# Revit family: PRD_AR_FlshCntrlDvcs_F5EWcFlushValve_F5EF4002
name_source: partatom
category: Plumbing Fixtures
units: mm (PartAtom-declared; Revit-internal decimal feet)

## family parameters
Cut with Voids When Loaded = Yes
Enable Cutting in Views = Yes
Host = Face
Maintain Annotation Orientation = No
OmniClass Number = 23.45.55.11
OmniClass Title = Sanitary Components
Part Type = Normal
Room Calculation Point = No
Round Connector Dimension = Use Diameter
Shared = No

## types (1)
- F5EF4002
    AssetType = Fixed
    BIMObjectName = PRD_AR_FlushControlDevices_F5EWcFlushValve_F5EF4002
    BodyMaterial = PRD_AR_PolishedChromium_PlatedBrass
    BottomMaterial = PRD_AR_Plastic_Black
    CW Connection = Yes
    CWFU = 0
    CalculationFlowRateColdWater = 1 l/s
    Category = Pr_75_50_46_31, Flush control devices
    CloseOffRating = 0.0 Pa
    DN = 20 mm  [stored 0.0656168 ft]
    Default Elevation = 1219 mm
    DefaultAutomaticHygieneFlush = 24h after the last activity
    Description = F5E WC flush valve DN 20 for concealed mounting, opto-electronically controlled. With circular sensor (diameter 55 mm), integrated control electronics and cleaning deactivation. Manufactured from polished chromium-plated brass, designed to be screwed from the rear, with anti-twist protection and solenoid flusher with extension cable for solenoid valve (length 5 m). Activated hygiene flushing 24 hours after last activation and saving of statistical data. With option for parametrisation and communication via optional bidirectional remote control. Options for battery operation with 6 V lithium battery (CR-P2) per fitting or separate power supply via power supply unit 6.75 V/12 V DC or AQUA 3000 open system accessories.

Battery compartment including battery or power supply unit with extension cable must be ordered separately.
    DiameterNominal = DN 20
    Export Type to IFC As = IfcValveType
    Features = Activated hygiene flushing 24 hours after last activation and saving of statistical data. With option for parametrisation and communication via optional bidirectional remote control.
    Finish = Chromed
    Flow = 0.0 L/s
    FlowCoefficient = 1 l/s
    FlushingRate = 1.3 L/s
    FunctionalPrinciple = electronic self-closing
    HW Connection = Yes
    HWFU = 0
    HasIntegralShutOffDevice = Yes
    IfcExportAs = IfcValveType
    IfcExportType = FLUSHING
    IsHighPressure = No
    Manufacturer = KWC Group Management AG
    ManufacturerName = KWC Group Management AG
    ManufacturerURL = www.kwc-professional.com
    Material = Polished chromium-plated brass
    MaterialCasing = brass-look
    MaterialFitting = brass-look
    MaximumFlowPressure = 4 bar
    MaximumFlushWaterVolume = 9 Liter
    MaximumFlushingFlow = 1.3 l/s
    MinimumFlowPressure = 1.2 bar
    MinimumFlushWaterVolume = 6 Liter
    MinimumFlushingFlow = 1 l/s
    Model = F5EF4002
    ModelNumber = 2030062326
    ModelReference = F5EF4002
    NBSDescription = Flush control devices
    NBSReference = 90-15-35/470
    Name = F5E WC flush valve F5EF4002
    NominalDepth = 0 mm  [stored 0 ft]
    NominalHeight = 55 mm  [stored 0.180446 ft]
    NominalWidth = 55 mm  [stored 0.180446 ft]
    Parameterization = remote control
    PowerConsumption = 3.5 Voltampere
    PowerSupplyConnection = 6,75 / 12 V DC / A3000 open
    ProductInformation = http://pim.kwc.com
    ProtectiveShutdown = Yes
    Size = 20
    SoundInsulation = No
    Status = New
    SurfaceFinishCasing = chromed
    TestPressure = 0.0 Pa
    Type IFC Predefined Type = FLUSHING
    TypeOfFlushingFitting = WC flush valve
    TypeOfMounting = concealed
    TypeOfOperation = sensor operation
    TypeOfPowerSupply = Transformer
    TypeOfSensor = opto-electronic sensor
    URL = www.kwc-professional.com
    Uniclass2015Code = Pr_75_50_46_31
    Uniclass2015Title = Flush control devices
    Uniclass2015Version = Products v1.36
    ValveMechanism = OTHER
    ValveOperation = SOLENOID
    ValvePattern = STRAIGHT_2_PORT
    Vent Connection = Yes
    Version = 1
    WFU = 0
    Waste Connection = Yes
    WorkingPressure = 0.0 Pa

note: [stored X ft] marks values corroborated as IEEE doubles in the binary element streams (Revit-internal decimal feet)

## geometry (parser evidence)
native form markers: Sweep x8
no freeform markers — native parametric forms only
